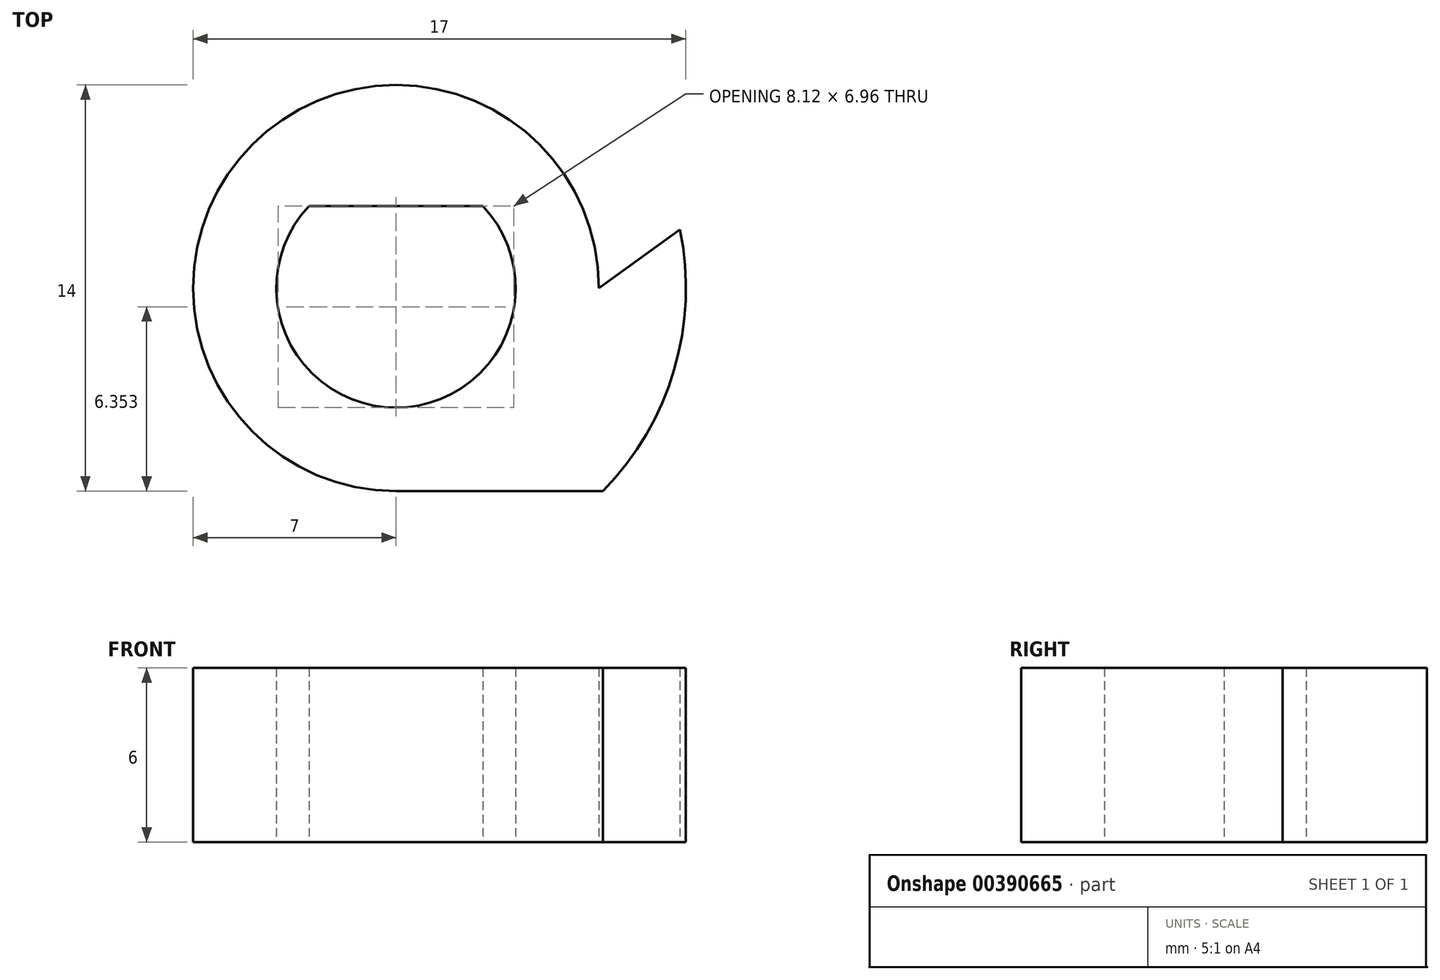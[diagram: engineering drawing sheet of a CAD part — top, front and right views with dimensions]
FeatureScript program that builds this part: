
annotation { "Feature Type Name" : "Feature", "Feature Type Description" : "" }
export const myFeature = defineFeature(function(context is Context, id is Id, definition is map)
    precondition{}
    {
        {
            var Q0;
            Q0=qCreatedBy(makeId("Top.planeOp"),FACE);
            var sketch = newSketch(context, id + "F0", { "sketchPlane" : qUnion([Q0])});
            skCircle(sketch, "E0", {"center": v(0, 0) * mm, "radius": 4.12 * mm});
            skLineSegment(sketch, "E1", {"start": v(-3, 2.83) * mm, "end": v(3, 2.83) * mm});
            skCircle(sketch, "E2", {"center": v(0, 0) * mm, "radius": 10 * mm});
            skCircle(sketch, "E3", {"center": v(0, 0) * mm, "radius": 7 * mm});
            skLineSegment(sketch, "E4", {"start": v(7, 0) * mm, "end": v(9.8, 2.02) * mm});
            skLineSegment(sketch, "E5", {"start": v(0, -7) * mm, "end": v(7.14, -7) * mm});
            skSolve(sketch);
        }
        {
            var Q0;
            {var subQ0=sQuery(id+"F0.wireOp",EDGE,"E1");var subQ1=sQuery(id+"F0.wireOp",EDGE,"E0");var subQ2=makeQuery(id+"F0.imprint","INTERSECT",VERTEX,{"disambiguationData":[OD(0.0)],"derivedFrom":[subQ1,subQ0]});Q0=makeQuery(id+"F0.imprint","IMPRINT",FACE,{"disambiguationData":[TD([[makeQuery(id+"F0.imprint","IMPRINT",EDGE,{"disambiguationData":[TD([[subQ2,1.0]])],"derivedFrom":subQ1}),-1.0]])]});}
            var Q1;
            {var subQ0=sQuery(id+"F0.wireOp",EDGE,"E1");Q1=makeQuery(id+"F0.imprint","IMPRINT",FACE,{"disambiguationData":[TD([[makeQuery(id+"F0.imprint","IMPRINT",EDGE,{"derivedFrom":subQ0}),1.0]])]});}
            var Q2;
            {var subQ0=sQuery(id+"F0.wireOp",EDGE,"GM1yE2Qi-p1sV-dTTT-ZE0t-593WRWt3D8od");Q2=makeQuery(id+"F0.imprint","IMPRINT",FACE,{"disambiguationData":[TD([[makeQuery(id+"F0.imprint","IMPRINT",EDGE,{"derivedFrom":subQ0}),-1.0]])]});}
            var Q3;
            {var subQ0=sQuery(id+"F0.wireOp",EDGE,"E4");Q3=makeQuery(id+"F0.imprint","IMPRINT",FACE,{"disambiguationData":[TD([[makeQuery(id+"F0.imprint","IMPRINT",EDGE,{"derivedFrom":subQ0}),-1.0]])]});}
            extrude(context, id + "F1", {"entities" : qUnion([Q0, Q1, Q2, Q3]), "offsetDistance" : 25 * mm, "depth" : 6 * mm});
        }
    });
